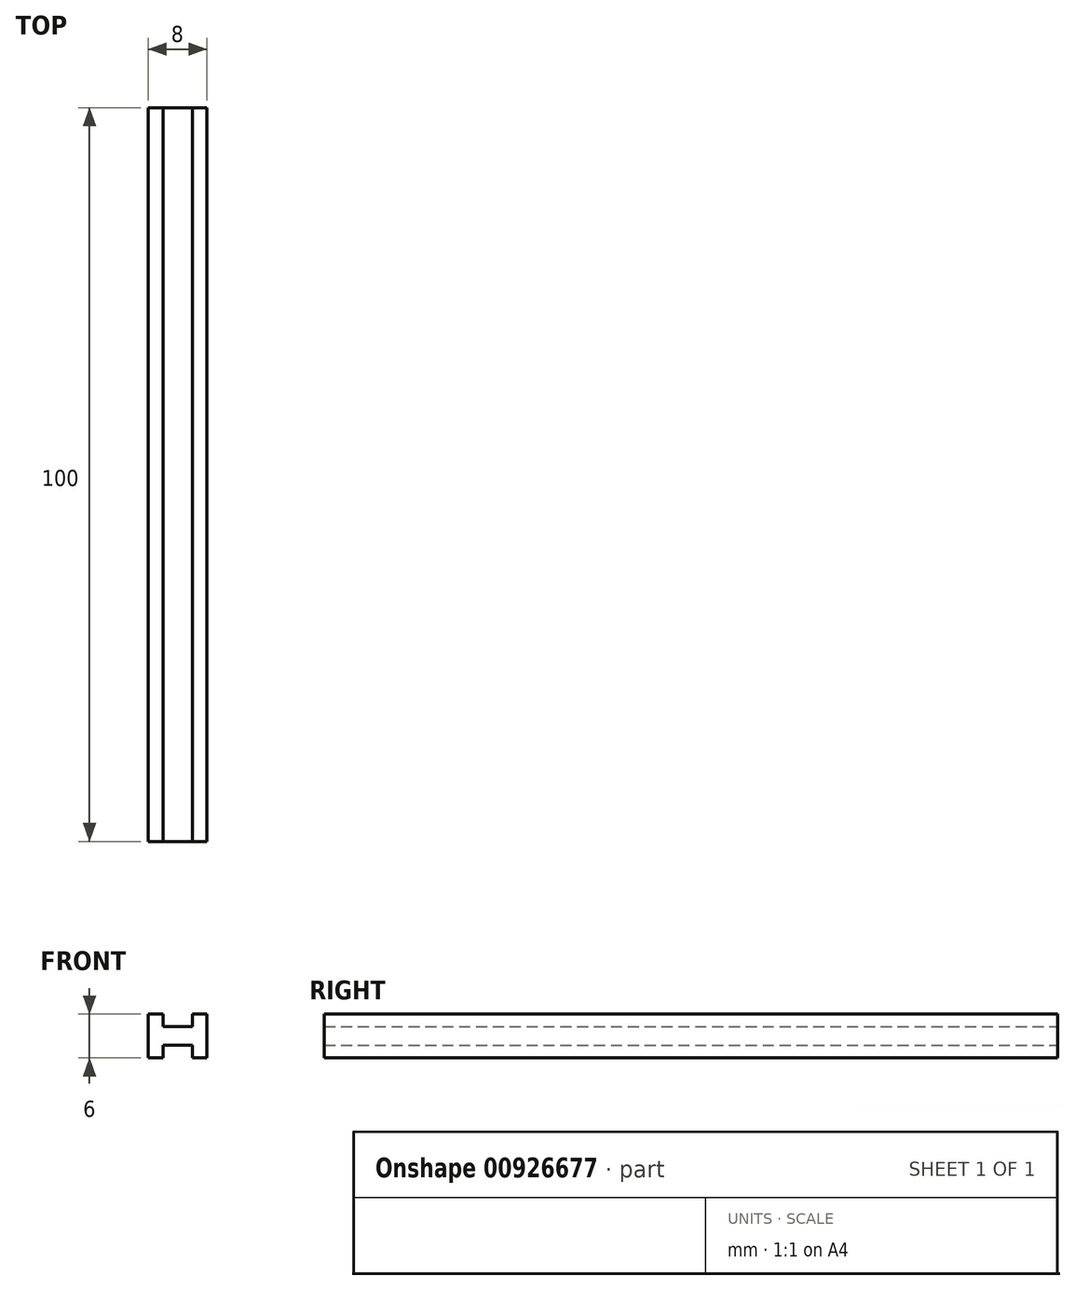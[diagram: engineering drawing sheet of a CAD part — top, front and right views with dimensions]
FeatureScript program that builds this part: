
annotation { "Feature Type Name" : "Feature", "Feature Type Description" : "" }
export const myFeature = defineFeature(function(context is Context, id is Id, definition is map)
    precondition{}
    {
        {
            var Q0;
            Q0=qCreatedBy(makeId("Front.planeOp"),FACE);
            var sketch = newSketch(context, id + "F0", { "sketchPlane" : qUnion([Q0])});
            skLineSegment(sketch, "E0.left", {"start": v(0, 0) * mm, "end": v(0, 6) * mm});
            skLineSegment(sketch, "E0.right", {"start": v(8, 0) * mm, "end": v(8, 6) * mm});
            skLineSegment(sketch, "E1", {"start": v(0, 6) * mm, "end": v(2, 6) * mm});
            skLineSegment(sketch, "E2.top", {"start": v(2, 4.25) * mm, "end": v(6, 4.25) * mm});
            skLineSegment(sketch, "E2.left", {"start": v(2, 6) * mm, "end": v(2, 4.25) * mm});
            skLineSegment(sketch, "E2.right", {"start": v(6, 6) * mm, "end": v(6, 4.25) * mm});
            skLineSegment(sketch, "E3", {"start": v(0, 0) * mm, "end": v(2, 0) * mm});
            skLineSegment(sketch, "E4.top", {"start": v(2, 1.75) * mm, "end": v(6, 1.75) * mm});
            skLineSegment(sketch, "E4.left", {"start": v(2, 0) * mm, "end": v(2, 1.75) * mm});
            skLineSegment(sketch, "E4.right", {"start": v(6, 0) * mm, "end": v(6, 1.75) * mm});
            skLineSegment(sketch, "E5", {"start": v(6, 6) * mm, "end": v(8, 6) * mm});
            skLineSegment(sketch, "E6", {"start": v(6, 0) * mm, "end": v(8, 0) * mm});
            skSolve(sketch);
        }
        {
            var Q0;
            Q0=makeQuery(id+"F0.imprint","IMPRINT",FACE,{"disambiguationData":[TD([[makeQuery(id+"F0.imprint","IMPRINT",EDGE,{"derivedFrom":sQuery(id+"F0.wireOp",EDGE,"E0.left")}),-1.0]])]});
            extrude(context, id + "F1", {"entities" : qUnion([Q0]), "depth" : 100 * mm, "offsetDistance" : 25 * mm});
        }
    });
